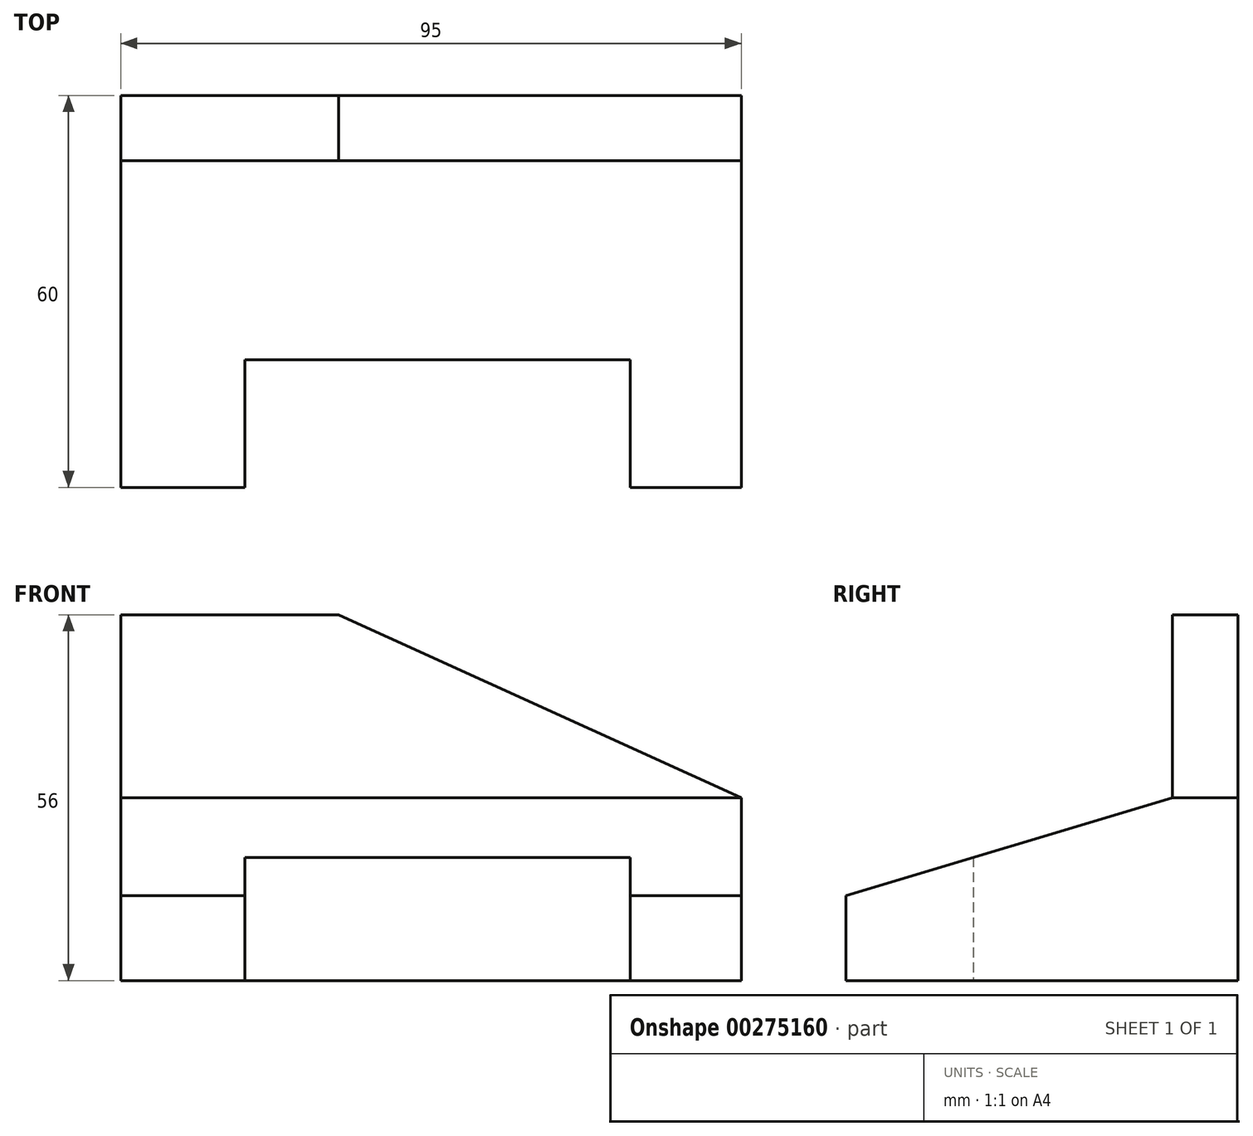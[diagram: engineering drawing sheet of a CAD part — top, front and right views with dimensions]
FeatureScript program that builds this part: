
annotation { "Feature Type Name" : "Feature", "Feature Type Description" : "" }
export const myFeature = defineFeature(function(context is Context, id is Id, definition is map)
    precondition{}
    {
        {
            var Q0;
            Q0=qCreatedBy(makeId("Right.planeOp"),FACE);
            var sketch = newSketch(context, id + "F0", { "sketchPlane" : qUnion([Q0])});
            skLineSegment(sketch, "E0", {"start": v(22.3, 2.4) * mm, "end": v(22.3, 58.4) * mm});
            skLineSegment(sketch, "E1", {"start": v(22.3, 58.4) * mm, "end": v(12.3, 58.4) * mm});
            skLineSegment(sketch, "E2", {"start": v(12.3, 58.4) * mm, "end": v(12.3, 30.4) * mm});
            skLineSegment(sketch, "E3", {"start": v(12.3, 30.4) * mm, "end": v(-37.7, 15.4) * mm});
            skLineSegment(sketch, "E4", {"start": v(-37.7, 15.4) * mm, "end": v(-37.7, 2.4) * mm});
            skLineSegment(sketch, "E5", {"start": v(-37.7, 2.4) * mm, "end": v(22.3, 2.4) * mm});
            skSolve(sketch);
        }
        {
            var Q0;
            Q0=makeQuery(id+"F0.imprint","IMPRINT",FACE,{"disambiguationData":[TD([[makeQuery(id+"F0.imprint","IMPRINT",EDGE,{"derivedFrom":sQuery(id+"F0.wireOp",EDGE,"E0")}),1.0]])]});
            var Q1;
            Q1 = qSketchRegion(id + "F2", true);
            extrude(context, id + "F1", {"entities" : qUnion([Q0, Q1]), "depth" : 95 * mm});
        }
        {
            var Q0;
            Q0=makeQuery(id+"F1.opExtrude","SWEPT_FACE",FACE,{"disambiguationData":[OSD([sQuery(id+"F0.wireOp",EDGE,"E2")])]});
            var sketch = newSketch(context, id + "F2", { "sketchPlane" : qUnion([Q0])});
            skLineSegment(sketch, "E6", {"start": v(33.37, 58.4) * mm, "end": v(95, 30.4) * mm});
            skSolve(sketch);
        }
        {
            var Q0;
            Q0=makeQuery(id+"F1.opExtrude","SWEPT_FACE",FACE,{"disambiguationData":[OSD([sQuery(id+"F0.wireOp",EDGE,"E5")])]});
            var sketch = newSketch(context, id + "F3", { "sketchPlane" : qUnion([Q0])});
            skLineSegment(sketch, "E7.bottom", {"start": v(19, 37.7) * mm, "end": v(78, 37.7) * mm});
            skLineSegment(sketch, "E7.top", {"start": v(19, 18.18) * mm, "end": v(78, 18.18) * mm});
            skLineSegment(sketch, "E7.left", {"start": v(19, 37.7) * mm, "end": v(19, 18.18) * mm});
            skLineSegment(sketch, "E7.right", {"start": v(78, 37.7) * mm, "end": v(78, 18.18) * mm});
            skSolve(sketch);
        }
        {
            var Q0;
            {var subQ0=sQuery(id+"F2.wireOp",EDGE,"E6");Q0=makeQuery(id+"F2.imprint","IMPRINT",FACE,{"disambiguationData":[TD([[makeQuery(id+"F2.imprint","IMPRINT",EDGE,{"derivedFrom":subQ0}),1.0]])]});}
            extrude(context, id + "F4", {"entities" : qUnion([Q0]), "operationType" : NewBodyOperationType.REMOVE, "oppositeDirection" : true, "depth" : 25 * mm});
        }
        {
            var Q0;
            Q0=makeQuery(id+"F3.imprint","IMPRINT",FACE,{"disambiguationData":[TD([[makeQuery(id+"F3.imprint","IMPRINT",EDGE,{"derivedFrom":sQuery(id+"F3.wireOp",EDGE,"E7.bottom")}),1.0]])]});
            extrude(context, id + "F5", {"entities" : qUnion([Q0]), "operationType" : NewBodyOperationType.REMOVE, "oppositeDirection" : true, "depth" : 25 * mm});
        }
    });
